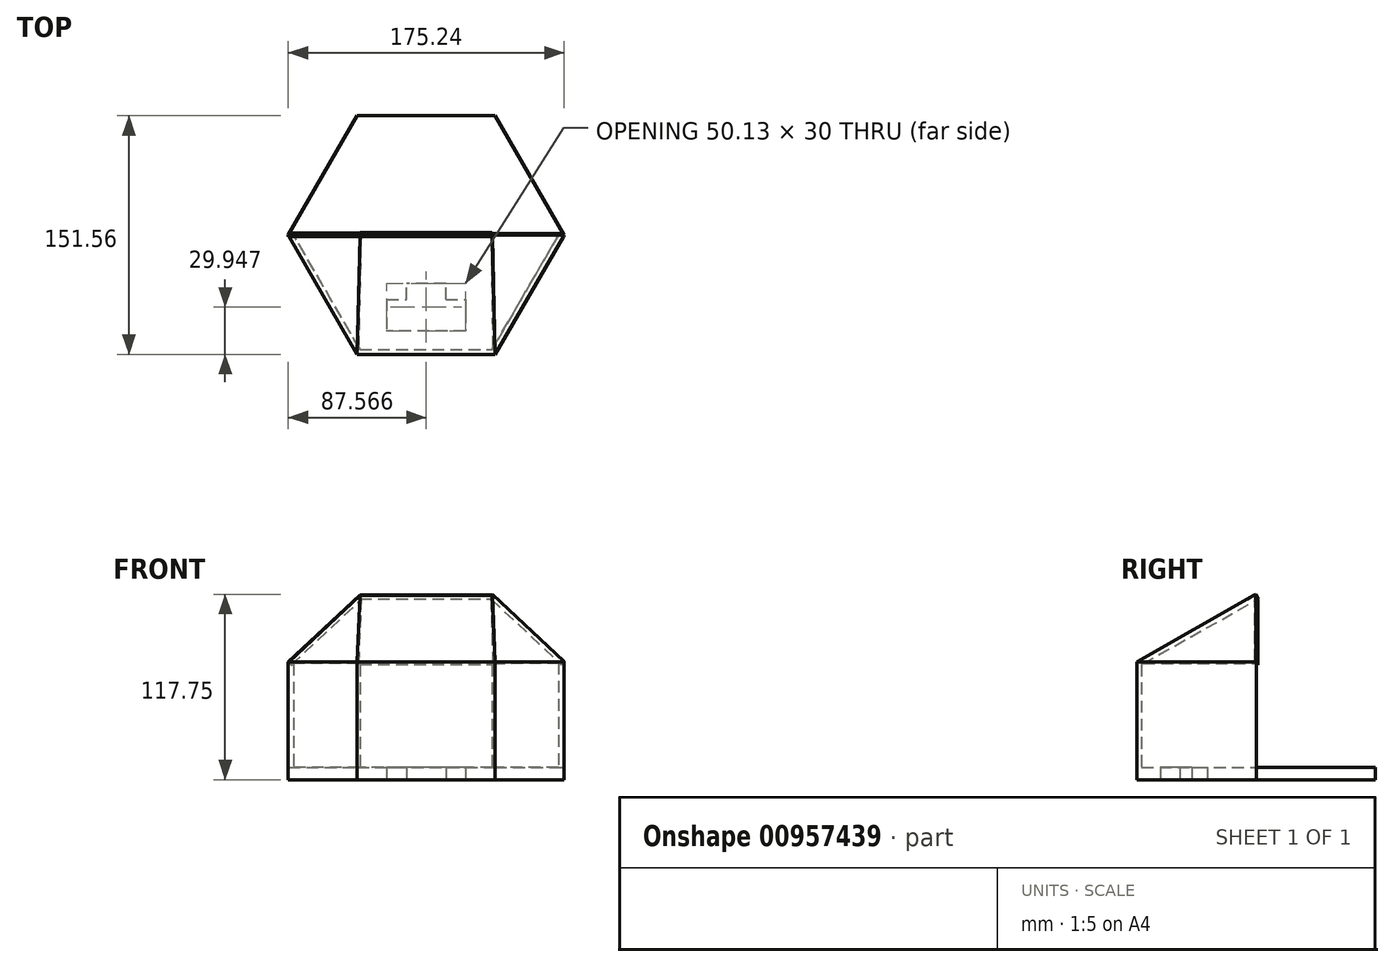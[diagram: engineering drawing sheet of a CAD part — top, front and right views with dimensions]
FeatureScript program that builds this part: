
annotation { "Feature Type Name" : "Feature", "Feature Type Description" : "" }
export const myFeature = defineFeature(function(context is Context, id is Id, definition is map)
    precondition{}
    {
        {
            var Q0;
            Q0=qCreatedBy(makeId("Top.planeOp"),FACE);
            var sketch = newSketch(context, id + "F0", { "sketchPlane" : qUnion([Q0])});
            skCircle(sketch, "E0.cCircle", {"center": v(0, 0) * mm, "radius": 75.78 * mm, "construction": true});
            skLineSegment(sketch, "E0.0", {"start": v(-43.75, 75.78) * mm, "end": v(43.75, 75.78) * mm});
            skLineSegment(sketch, "E0.1", {"start": v(43.75, 75.78) * mm, "end": v(87.5, 0) * mm});
            skLineSegment(sketch, "E0.2", {"start": v(87.5, 0) * mm, "end": v(43.75, -75.78) * mm});
            skLineSegment(sketch, "E0.3", {"start": v(43.75, -75.78) * mm, "end": v(-43.75, -75.78) * mm});
            skLineSegment(sketch, "E0.4", {"start": v(-43.75, -75.78) * mm, "end": v(-87.5, 0) * mm});
            skLineSegment(sketch, "E0.5", {"start": v(-87.5, 0) * mm, "end": v(-43.75, 75.78) * mm});
            skPoint(sketch, "E0.0.midPoint", {"position": v(0, 75.78) * mm});
            skLineSegment(sketch, "E1.0", {"start": v(-84.04, 0) * mm, "end": v(-42.02, 72.78) * mm});
            skLineSegment(sketch, "E1.1", {"start": v(42.02, 72.78) * mm, "end": v(84.04, 0) * mm});
            skLineSegment(sketch, "E1.2", {"start": v(84.04, 0) * mm, "end": v(42.02, -72.78) * mm});
            skLineSegment(sketch, "E1.3", {"start": v(-42.02, 72.78) * mm, "end": v(42.02, 72.78) * mm});
            skLineSegment(sketch, "E1.4", {"start": v(42.02, -72.78) * mm, "end": v(-42.02, -72.78) * mm});
            skLineSegment(sketch, "E1.5", {"start": v(-42.02, -72.78) * mm, "end": v(-84.04, 0) * mm});
            skLineSegment(sketch, "E2", {"start": v(-87.5, 0) * mm, "end": v(-84.04, 0) * mm});
            skLineSegment(sketch, "E3", {"start": v(84.04, 0) * mm, "end": v(87.5, 0) * mm});
            skLineSegment(sketch, "E4", {"start": v(0, 0) * mm, "end": v(0, 72.78) * mm, "construction": true});
            skLineSegment(sketch, "E5", {"start": v(0, 0) * mm, "end": v(42.02, 72.78) * mm, "construction": true});
            skLineSegment(sketch, "E6", {"start": v(0, 0) * mm, "end": v(-42.02, 72.78) * mm, "construction": true});
            skLineSegment(sketch, "E7", {"start": v(0, 36.39) * mm, "end": v(0, 72.78) * mm, "construction": true});
            skLineSegment(sketch, "E8.bottom", {"start": v(25, 48.33) * mm, "end": v(-25, 48.33) * mm});
            skLineSegment(sketch, "E8.top", {"start": v(25, 60.83) * mm, "end": v(-25, 60.83) * mm});
            skLineSegment(sketch, "E8.left", {"start": v(25, 48.33) * mm, "end": v(25, 60.83) * mm});
            skLineSegment(sketch, "E8.right", {"start": v(-25, 48.33) * mm, "end": v(-25, 60.83) * mm});
            skPoint(sketch, "E8.middle", {"position": v(0, 54.58) * mm});
            skLineSegment(sketch, "E9", {"start": v(0, 0) * mm, "end": v(38.98, 0) * mm, "construction": true});
            skLineSegment(sketch, "E10.MirrorCS", {"start": v(25, -48.33) * mm, "end": v(25, -60.83) * mm});
            skLineSegment(sketch, "E11.MirrorCS", {"start": v(25, -60.83) * mm, "end": v(-25, -60.83) * mm});
            skLineSegment(sketch, "E12.MirrorCS", {"start": v(-25, -48.33) * mm, "end": v(-25, -60.83) * mm});
            skLineSegment(sketch, "E13", {"start": v(-25, -48.33) * mm, "end": v(-25, -40.83) * mm});
            skLineSegment(sketch, "E14", {"start": v(-25, -40.83) * mm, "end": v(25.13, -40.83) * mm});
            skLineSegment(sketch, "E15", {"start": v(25.13, -40.83) * mm, "end": v(25, -48.33) * mm});
            skLineSegment(sketch, "E16", {"start": v(25.13, -40.83) * mm, "end": v(0, -40.83) * mm, "construction": true});
            skLineSegment(sketch, "E17", {"start": v(0, -40.83) * mm, "end": v(-25, -40.83) * mm, "construction": true});
            skLineSegment(sketch, "E18", {"start": v(0, -40.83) * mm, "end": v(12.57, -40.83) * mm, "construction": true});
            skLineSegment(sketch, "E19", {"start": v(12.57, -40.83) * mm, "end": v(12.57, -30.83) * mm});
            skLineSegment(sketch, "E20", {"start": v(12.57, -30.83) * mm, "end": v(-12.5, -30.83) * mm});
            skLineSegment(sketch, "E21", {"start": v(0, -40.83) * mm, "end": v(-12.5, -40.83) * mm});
            skLineSegment(sketch, "E22", {"start": v(-12.5, -40.83) * mm, "end": v(-12.5, -30.83) * mm});
            skSolve(sketch);
        }
        {
            var Q0;
            Q0=makeQuery(id+"F0.imprint","IMPRINT",FACE,{"disambiguationData":[TD([[makeQuery(id+"F0.imprint","IMPRINT",EDGE,{"derivedFrom":sQuery(id+"F0.wireOp",EDGE,"E1.0")}),-1.0]])]});
            extrude(context, id + "F1", {"entities" : qUnion([Q0]), "depth" : 8 * mm, "offsetDistance" : 25 * mm});
        }
        {
            var Q0;
            Q0=makeQuery(id+"F0.imprint","IMPRINT",FACE,{"disambiguationData":[TD([[makeQuery(id+"F0.imprint","IMPRINT",EDGE,{"derivedFrom":sQuery(id+"F0.wireOp",EDGE,"E0.2")}),-1.0]])]});
            extrude(context, id + "F2", {"entities" : qUnion([Q0]), "operationType" : NewBodyOperationType.ADD, "depth" : 75 * mm, "offsetDistance" : 25 * mm});
        }
        {
            var Q0;
            Q0=qCreatedBy(makeId("Front.planeOp"),FACE);
            var sketch = newSketch(context, id + "F3", { "sketchPlane" : qUnion([Q0])});
            skLineSegment(sketch, "E23", {"start": v(0, 0) * mm, "end": v(0, 144.27) * mm, "construction": true});
            skLineSegment(sketch, "E24", {"start": v(0, 144.27) * mm, "end": v(-94, 144.27) * mm, "construction": true});
            skLineSegment(sketch, "E25", {"start": v(0, 144.27) * mm, "end": v(81.74, 144.27) * mm});
            skLineSegment(sketch, "E26", {"start": v(0, 0) * mm, "end": v(0, 75) * mm, "construction": true});
            skLineSegment(sketch, "E27", {"start": v(0, 75) * mm, "end": v(0, 114.5) * mm, "construction": true});
            skLineSegment(sketch, "E28", {"start": v(0, 75) * mm, "end": v(-87.5, 75) * mm, "construction": true});
            skLineSegment(sketch, "E29", {"start": v(0, 114.5) * mm, "end": v(42.02, 114.5) * mm, "construction": true});
            skLineSegment(sketch, "E30", {"start": v(0, 114.5) * mm, "end": v(-42.02, 114.5) * mm});
            skLineSegment(sketch, "E31", {"start": v(0, 75) * mm, "end": v(-84.04, 75) * mm, "construction": true});
            skLineSegment(sketch, "E32", {"start": v(-42.02, 114.5) * mm, "end": v(-84.04, 75) * mm});
            skLineSegment(sketch, "E33", {"start": v(-42.02, 114.5) * mm, "end": v(-42.02, 117.5) * mm, "construction": true});
            skLineSegment(sketch, "E34", {"start": v(-42.02, 117.5) * mm, "end": v(-87.5, 75) * mm});
            skLineSegment(sketch, "E35", {"start": v(-42.02, 117.5) * mm, "end": v(0, 117.5) * mm});
            skLineSegment(sketch, "E36.MirrorCS", {"start": v(42.02, 117.5) * mm, "end": v(87.5, 75) * mm});
            skLineSegment(sketch, "E37.MirrorCS", {"start": v(42.02, 114.5) * mm, "end": v(84.04, 75) * mm});
            skLineSegment(sketch, "E38.MirrorCS", {"start": v(42.02, 117.5) * mm, "end": v(0, 117.5) * mm});
            skLineSegment(sketch, "E39.MirrorCS", {"start": v(0, 114.5) * mm, "end": v(42.02, 114.5) * mm});
            skLineSegment(sketch, "E40", {"start": v(87.5, 75) * mm, "end": v(84.04, 75) * mm});
            skLineSegment(sketch, "E41", {"start": v(-84.04, 75) * mm, "end": v(-87.5, 75) * mm});
            skSolve(sketch);
        }
        {
            var Q0;
            Q0=makeQuery(id+"F0.imprint","IMPRINT",FACE,{"disambiguationData":[TD([[makeQuery(id+"F0.imprint","IMPRINT",EDGE,{"derivedFrom":sQuery(id+"F0.wireOp",EDGE,"E0.0")}),-1.0]])]});
            extrude(context, id + "F4", {"entities" : qUnion([Q0]), "operationType" : NewBodyOperationType.ADD, "oppositeDirection" : true, "depth" : -8 * mm, "offsetDistance" : 25 * mm});
        }
        {
            var Q0;
            Q0=makeQuery(id+"F2.opExtrude","CAP_EDGE",EDGE,{"disambiguationData":[OSD([sQuery(id+"F0.wireOp",EDGE,"E0.3")])],"isStart":false});
            var Q1;
            Q1=sQuery(id+"F3.wireOp",VERTEX,"E35.end");
            cPlane(context, id + "F5", {"entities" : qUnion([Q0, Q1]), "cplaneType" : CPlaneType.LINE_ANGLE, "offset" : 25 * mm, "angle" : 0 * degree, "width" : 150 * mm, "height" : 150 * mm});
        }
        {
            var Q0;
            Q0=qCreatedBy(id+"F5.planeOp",FACE);
            var sketch = newSketch(context, id + "F6", { "sketchPlane" : qUnion([Q0])});
            skLineSegment(sketch, "E42", {"start": v(0, 29.4) * mm, "end": v(43.75, 29.4) * mm});
            skLineSegment(sketch, "E43", {"start": v(0, 29.4) * mm, "end": v(-43.75, 29.4) * mm});
            skLineSegment(sketch, "E44", {"start": v(-43.75, 29.4) * mm, "end": v(-42.02, -57.48) * mm});
            skLineSegment(sketch, "E45", {"start": v(43.75, 29.4) * mm, "end": v(42.02, -57.48) * mm});
            skLineSegment(sketch, "E46", {"start": v(-42.02, -57.48) * mm, "end": v(42.02, -57.48) * mm});
            skSolve(sketch);
        }
        {
            var Q0;
            Q0=makeQuery(id+"F6.imprint","IMPRINT",FACE,{"disambiguationData":[TD([[makeQuery(id+"F6.imprint","IMPRINT",EDGE,{"derivedFrom":sQuery(id+"F6.wireOp",EDGE,"E42")}),-1.0]])]});
            extrude(context, id + "F7", {"entities" : qUnion([Q0]), "operationType" : NewBodyOperationType.ADD, "depth" : 3 * mm, "offsetDistance" : 25 * mm});
        }
        {
            var Q0;
            Q0=makeQuery(id+"F3.imprint","IMPRINT",FACE,{"disambiguationData":[TD([[makeQuery(id+"F3.imprint","IMPRINT",EDGE,{"derivedFrom":sQuery(id+"F3.wireOp",EDGE,"E30")}),-1.0]])]});
            extrude(context, id + "F8", {"entities" : qUnion([Q0]), "operationType" : NewBodyOperationType.ADD, "depth" : 1 * mm, "offsetDistance" : 25 * mm});
        }
        {
            var Q0;
            Q0=makeQuery(id+"F8.opExtrude","CAP_EDGE",EDGE,{"disambiguationData":[OSD([sQuery(id+"F3.wireOp",EDGE,"E34")])],"isStart":true});
            var Q1;
            Q1=makeQuery(id+"F7.boolean.opBoolean","MERGE",VERTEX,{"derivedFrom":[makeQuery(id+"F2.opExtrude","CAP_VERTEX",VERTEX,{"disambiguationData":[OSD([sQuery(id+"F0.wireOp",EDGE,"E0.3"),sQuery(id+"F0.wireOp",EDGE,"E0.4")])],"isStart":false}),makeQuery(id+"F7.opExtrude","CAP_VERTEX",VERTEX,{"disambiguationData":[OSD([sQuery(id+"F6.wireOp",EDGE,"E43"),sQuery(id+"F6.wireOp",EDGE,"E44")])],"isStart":true})]});
            cPlane(context, id + "F9", {"entities" : qUnion([Q0, Q1]), "cplaneType" : CPlaneType.LINE_ANGLE, "offset" : 25 * mm, "angle" : 0 * degree, "width" : 150 * mm, "height" : 150 * mm});
        }
        {
            var Q0;
            Q0=qCreatedBy(id+"F9.planeOp",FACE);
            var sketch = newSketch(context, id + "F10", { "sketchPlane" : qUnion([Q0])});
            skLineSegment(sketch, "E47", {"start": v(-25.66, 35.61) * mm, "end": v(30.99, -31.08) * mm});
            skLineSegment(sketch, "E48", {"start": v(-25.66, 35.61) * mm, "end": v(33.23, 55.79) * mm});
            skLineSegment(sketch, "E49", {"start": v(33.23, 55.79) * mm, "end": v(30.99, -31.08) * mm});
            skSolve(sketch);
        }
        {
            var Q0;
            Q0=qSketchRegion(id+"F10",true);
            extrude(context, id + "F11", {"entities" : qUnion([Q0]), "operationType" : NewBodyOperationType.ADD, "depth" : -3 * mm, "offsetDistance" : 25 * mm});
        }
        {
            var Q0;
            Q0=makeQuery(id+"F8.opExtrude","CAP_EDGE",EDGE,{"disambiguationData":[OSD([sQuery(id+"F3.wireOp",EDGE,"E36.MirrorCS")])],"isStart":false});
            var Q1;
            Q1=makeQuery(id+"F7.boolean.opBoolean","MERGE",VERTEX,{"derivedFrom":[makeQuery(id+"F2.opExtrude","CAP_VERTEX",VERTEX,{"disambiguationData":[OSD([sQuery(id+"F0.wireOp",EDGE,"E0.2"),sQuery(id+"F0.wireOp",EDGE,"E0.3")])],"isStart":false}),makeQuery(id+"F7.opExtrude","CAP_VERTEX",VERTEX,{"disambiguationData":[OSD([sQuery(id+"F6.wireOp",EDGE,"E42"),sQuery(id+"F6.wireOp",EDGE,"E45")])],"isStart":true})]});
            cPlane(context, id + "F12", {"entities" : qUnion([Q0, Q1]), "cplaneType" : CPlaneType.LINE_ANGLE, "offset" : 25 * mm, "angle" : 0 * degree, "width" : 150 * mm, "height" : 150 * mm});
        }
        {
            var Q0;
            Q0=qCreatedBy(id+"F12.planeOp",FACE);
            var sketch = newSketch(context, id + "F13", { "sketchPlane" : qUnion([Q0])});
            skLineSegment(sketch, "E50", {"start": v(-32.88, -56.36) * mm, "end": v(25.94, -35.98) * mm});
            skLineSegment(sketch, "E51", {"start": v(25.94, -35.98) * mm, "end": v(-30.94, 30.51) * mm});
            skLineSegment(sketch, "E52", {"start": v(-30.94, 30.51) * mm, "end": v(-32.88, -56.36) * mm});
            skSolve(sketch);
        }
        {
            var Q0;
            Q0=qSketchRegion(id+"F13",true);
            extrude(context, id + "F14", {"entities" : qUnion([Q0]), "operationType" : NewBodyOperationType.ADD, "depth" : 3 * mm, "offsetDistance" : 25 * mm});
        }
        {
            var Q0;
            Q0=makeQuery(id+"F0.imprint","IMPRINT",FACE,{"disambiguationData":[TD([[makeQuery(id+"F0.imprint","IMPRINT",EDGE,{"derivedFrom":sQuery(id+"F0.wireOp",EDGE,"E8.bottom")}),-1.0]])]});
            extrude(context, id + "F15", {"entities" : qUnion([Q0]), "operationType" : NewBodyOperationType.ADD, "depth" : 8 * mm, "offsetDistance" : 25 * mm});
        }
        {
            var Q0;
            Q0=makeQuery(id+"F0.imprint","IMPRINT",FACE,{"disambiguationData":[TD([[makeQuery(id+"F0.imprint","IMPRINT",EDGE,{"derivedFrom":sQuery(id+"F0.wireOp",EDGE,"E10.MirrorCS")}),-1.0]])]});
            extrude(context, id + "F16", {"entities" : qUnion([Q0]), "operationType" : NewBodyOperationType.REMOVE, "oppositeDirection" : true, "depth" : 25 * mm, "offsetDistance" : 25 * mm});
        }
    });
